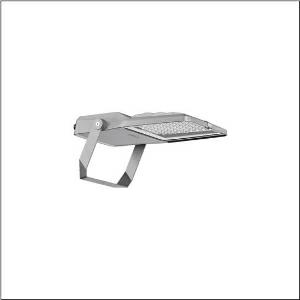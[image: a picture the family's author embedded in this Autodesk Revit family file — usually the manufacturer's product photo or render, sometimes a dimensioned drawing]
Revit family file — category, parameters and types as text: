
# Revit family: floodlight_fl_21_iq_mini___pl61_5xa7771d4c1a_f1b8
name_source: partatom
category: Lighting Fixtures
units: mm (PartAtom-declared; Revit-internal decimal feet)

## family parameters
Cut with Voids When Loaded = No
Host = Face
Light Source = No
Part Type = Normal
Room Calculation Point = No
Round Connector Dimension = Use Diameter
Shared = No

## types (1)
- --- (1 x LED, 18260 lm, 143 W, 4000K)
    Apparent Load = 143 VA
    CIE Flux Codes = 33 65 98 100 100
    Color Rendering = 70
    Color Temperature = 4000K
    Default Elevation = 1800 mm
    Description = Floodlight FL 21 iQ mini, floodlight, primary light control with lens, of PMMA, primary optical cover: protective disc, of toughened safety glass, transparent, light distribution: PL61, light emission: direct distribution, installation type: surface-mounted, LED, High Power LED, rated luminous flux: 18.260lm, luminous efficacy: 128lm/W, light colour: 740, colour temperature: 4000K, control gear: iQ Comfort/DALI, control: Auto-Match, Temp-Guard, Lumen-Switch, Night-Set, Smart-Wire, Light-Fading, Desk-Remote (wireless, voltage-free reading and setting of iQ features in the workshop via application-optimized NFC function/RFID function), optimised constant luminous flux control (CLO 2.0), with terminal, 6-pole, mains connection: 220..240V, AC, 50/60Hz, start of lifetime: 143W, end of service life: 152W, reduction: 61W, luminaire housing, of diecast aluminium, powder-coated, Siteco® metallic grey (DB 702S), corrosivity category C5 mid according to DIN EN ISO 12944, suitable for swimming pools, chlorine-resistant, sealing non-destructively replaceable, mounting bracket, of steel, galvanised, powder-coated, Siteco® metallic grey (DB 702S), protection rating (complete): IP66, insulation class (complete): insulation class II (safety insulation), certification: CE, ENEC, VDE, protection symbol: D, impact resistance: IK08, permissible operating ambient temperature: -40..+40°C, permissible operating ambient temperature for outdoor applications: -40..+50°C, standard: DIN EN 12944, LABS conformity tested according to VDMA 24364:2018-05, packaging unit: 1 piece

Light Distribution: PL61
    Height = 70 mm
    Lamp = 1 x LED
    Lamp Light Flux = 18260 lm
    Lamp Power = 143 W
    Lamp count = 1
    Length = 485 mm
    Luminous efficacy = 128 lm/W
    Manufacturer = Siteco
    ModVariant = No
    Model = 5XA7771D4C1A
    Number of Poles = 1
    OnlyDefault = Yes
    Power Factor = 1
    Product Name = Floodlight FL 21 iQ mini | PL61
    Product group = floodlight | pylon annexe
    ProductGroupID = 6200
    Protection Class = Protection class II
    Protection Degree = IP 66
    RLX_Detail_Level = 1
    RLX_Emergency_Light_Flux = 0 lm
    RLX_Emergency_Type = 0
    RLX_Emergency_Type_DB = No
    RlxData = <blob elided: 96641 chars, md5=74c9ac70>
    Socket = socket
    Standby Power = 0 W
    System Light Flux = 18260 lm
    System Power = 143 W
    Type Comments = factory setting: luminous flux: 100 % | dim-lin: 254 | 730 mA
    Type Image = l_1006845.jpg
    URL = http://relux.com
    VarID = @adj_172680
    Voltage = 0 V
    Weight = 0.00 kg
    Width = 337 mm

## geometry (parser evidence)
native form markers: Blend x4, Sweep x11
no freeform markers — native parametric forms only
